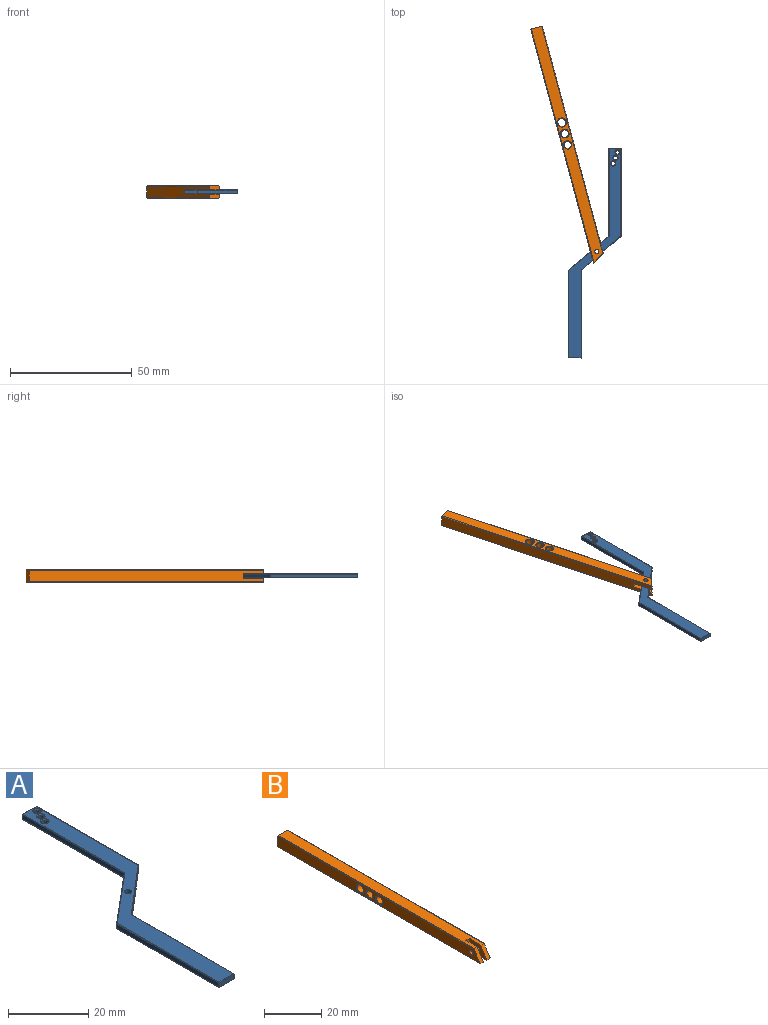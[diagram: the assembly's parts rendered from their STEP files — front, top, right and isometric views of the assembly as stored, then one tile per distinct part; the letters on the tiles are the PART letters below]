
ASSEMBLY  parts=2 mates=1
PART A: 51 faces, bbox 21.7x85.9x1.7 mm
  f0: plane 35.64x1.35mm, normal (1,0,0), area 48mm2, adj f8,f15,f37,f40
  f1: plane 4.92x1.35mm, normal (0.04,1,0), area 6.6mm2, adj f2,f13,f38,f40
  f2: plane 35.89x1.35mm, normal (-1,0,0), area 48.3mm2, adj f1,f11,f32,f36
  f3: plane 16.55x13.86mm, normal (-0.64,0.77,0), area 29.1mm2, adj f12,f25,f31,f32
  f4: plane 35.79x1.35mm, normal (-1,0,0), area 48.2mm2, adj f14,f20,f24,f25
  f5: plane 5.1x1.35mm, normal (0,-1,0), area 6.9mm2, adj f16,f20,f26,f27
  f6: plane 35.86x1.35mm, normal (1,0,0), area 48.3mm2, adj f8,f18,f26,f33
  f7: cylinder r=0.89mm len=1.79mm, axis (0,0,-1), area 9.3mm2, adj f9,f10
  f8: plane 16.32x13.95mm, normal (0.65,-0.76,0), area 28.9mm2, adj f0,f6,f17,f35
  f9: plane 85.62x21.41mm, normal (0,0,1), area 406mm2, adj f7,f24,f27,f31,f33,f34,f35,f36
  f10: plane 85.62x21.41mm, normal (0,0,-1), area 406mm2, adj f7,f11,f12,f13,f14,f15,f16,f17
  f11: cylinder r=0.15mm len=36.03mm, axis (0,-1,0), area 8.6mm2, adj f2,f10,f13,f29
  f12: cylinder r=0.15mm len=16.75mm, axis (-0.77,-0.64,0), area 5.2mm2, adj f3,f10,f21,f29
  f13: cylinder r=0.15mm len=4.92mm, axis (-1,0.04,0), area 1.2mm2, adj f1,f10,f11,f41
  f14: cylinder r=0.15mm len=35.79mm, axis (0,-1,0), area 8.6mm2, adj f4,f10,f19,f21
  f15: cylinder r=0.15mm len=35.64mm, axis (0,1,0), area 8.5mm2, adj f0,f10,f17,f41
  f16: cylinder r=0.15mm len=5.1mm, axis (1,0,0), area 1.2mm2, adj f5,f10,f19,f22
  f17: cylinder r=0.15mm len=16.47mm, axis (0.76,0.65,0), area 5.1mm2, adj f8,f10,f15,f18
  f18: cylinder r=0.15mm len=35.93mm, axis (0,1,0), area 8.6mm2, adj f6,f10,f17,f22
  f19: sphere r=0.15mm, area 0mm2, adj f14,f16,f20
  f20: cylinder r=0.15mm len=1.35mm, axis (0,0,-1), area 0.3mm2, adj f4,f5,f19,f23
  f21: sphere r=0.15mm, area 0mm2, adj f12,f14,f25
  f22: sphere r=0.15mm, area 0mm2, adj f16,f18,f26
  f23: sphere r=0.15mm, area 0mm2, adj f20,f24,f27
  f24: cylinder r=0.15mm len=35.79mm, axis (0,1,0), area 8.6mm2, adj f4,f9,f23,f28
  f25: cylinder r=0.15mm len=1.35mm, axis (0,0,-1), area 0.2mm2, adj f3,f4,f21,f28
  f26: cylinder r=0.15mm len=1.35mm, axis (0,0,-1), area 0.3mm2, adj f5,f6,f22,f30
  f27: cylinder r=0.15mm len=5.1mm, axis (-1,0,0), area 1.2mm2, adj f5,f9,f23,f30
  f28: sphere r=0.15mm, area 0mm2, adj f24,f25,f31
  f29: bspline ~0.21x0.17mm, area 0mm2, adj f11,f12,f32
  f30: sphere r=0.15mm, area 0mm2, adj f26,f27,f33
  f31: cylinder r=0.15mm len=16.64mm, axis (0.77,0.64,0), area 5.2mm2, adj f3,f9,f28,f34
  f32: cylinder r=0.15mm len=1.35mm, axis (0,0,1), area 0.2mm2, adj f2,f3,f29,f34
  f33: cylinder r=0.15mm len=35.93mm, axis (0,-1,0), area 8.6mm2, adj f6,f9,f30,f35
  f34: torus R=0.3mm, axis (0,0,1), area 0mm2, adj f9,f31,f32,f36
  f35: cylinder r=0.15mm len=16.47mm, axis (-0.76,-0.65,0), area 5.1mm2, adj f8,f9,f33,f37
  f36: cylinder r=0.15mm len=35.89mm, axis (0,1,0), area 8.6mm2, adj f2,f9,f34,f38
  f37: cylinder r=0.15mm len=35.64mm, axis (0,-1,0), area 8.5mm2, adj f0,f9,f35,f39
  f38: cylinder r=0.15mm len=4.92mm, axis (1,-0.04,0), area 1.2mm2, adj f1,f9,f36,f39
  f39: sphere r=0.15mm, area 0mm2, adj f37,f38,f40
  f40: cylinder r=0.15mm len=1.35mm, axis (0,0,-1), area 0.3mm2, adj f0,f1,f39,f41
  f41: sphere r=0.15mm, area 0mm2, adj f13,f15,f40
  f42: cylinder r=0.82mm len=1.65mm, axis (0,0,1), area 5.9mm2, adj f45,f50
  f43: cylinder r=0.81mm len=1.62mm, axis (0,0,1), area 5.8mm2, adj f46,f49
  f44: cylinder r=0.8mm len=1.61mm, axis (0,0,1), area 5.8mm2, adj f47,f48
  f45: torus R=1.08mm, axis (0,0,1), area 2.3mm2, adj f9,f42
  f46: torus R=1.06mm, axis (0,0,1), area 2.3mm2, adj f9,f43
  f47: torus R=1.06mm, axis (0,0,1), area 2.2mm2, adj f9,f44
  f48: torus R=1.06mm, axis (0,0,1), area 2.2mm2, adj f10,f44
  f49: torus R=1.06mm, axis (0,0,1), area 2.3mm2, adj f10,f43
  f50: torus R=1.08mm, axis (0,0,1), area 2.3mm2, adj f10,f42
PART B: 25 faces, bbox 5x99.5x5 mm
  f0: plane 99.32x4.45mm, normal (-1,0,0), area 402.8mm2, adj f2,f8,f10,f15,f16,f17,f22,f24
  f1: plane 99.32x4.45mm, normal (1,0,0), area 402.8mm2, adj f2,f9,f11,f18,f19,f20,f21,f23
  f2: plane 4.95x4.95mm, normal (0,1,0), area 24.5mm2, adj f0,f1,f3,f4,f21,f22,f23,f24
  f3: plane 96.46x4.44mm, normal (0,0,1), area 419.1mm2, adj f2,f5,f6,f7,f8,f9,f23,f24
  f4: plane 99.48x4.44mm, normal (0,0,-1), area 427.5mm2, adj f2,f5,f6,f7,f8,f9,f21,f22
  f5: plane 8.69x4.95mm, normal (-1,0,0), area 33.1mm2, adj f3,f4,f6,f9,f11
  f6: plane 4.95x1.67mm, normal (0,-1,0), area 8.3mm2, adj f3,f4,f5,f7
  f7: plane 8.69x4.95mm, normal (1,0,0), area 33.1mm2, adj f3,f4,f6,f8,f10
  f8: plane 4.95x3.01mm, normal (0,-0.85,0.52), area 9.5mm2, adj f0,f3,f4,f7,f22,f24
  f9: plane 4.95x3.01mm, normal (0,-0.85,0.52), area 9.5mm2, adj f1,f3,f4,f5,f21,f23
  f10: cylinder r=0.89mm len=1.78mm, axis (-1,0,0), area 9.2mm2, adj f0,f7
  f11: cylinder r=0.89mm len=1.78mm, axis (-1,0,0), area 9.2mm2, adj f1,f5
  f12: cylinder r=1.46mm len=4.44mm, axis (1,0,0), area 40.7mm2, adj f17,f18
  f13: cylinder r=1.52mm len=4.44mm, axis (1,0,0), area 42.4mm2, adj f16,f19
  f14: cylinder r=1.63mm len=4.44mm, axis (1,0,0), area 45.4mm2, adj f15,f20
  f15: torus R=1.88mm, axis (-1,0,0), area 4.3mm2, adj f0,f14
  f16: torus R=1.77mm, axis (-1,0,0), area 4mm2, adj f0,f13
  f17: torus R=1.71mm, axis (-1,0,0), area 3.9mm2, adj f0,f12
  f18: torus R=1.71mm, axis (-1,0,0), area 3.9mm2, adj f1,f12
  f19: torus R=1.77mm, axis (-1,0,0), area 4mm2, adj f1,f13
  f20: torus R=1.88mm, axis (-1,0,0), area 4.3mm2, adj f1,f14
  f21: cylinder r=0.25mm len=99.48mm, axis (0,1,0), area 39.7mm2, adj f1,f2,f4,f9
  f22: cylinder r=0.25mm len=99.48mm, axis (0,-1,0), area 39.7mm2, adj f0,f2,f4,f8
  f23: cylinder r=0.25mm len=96.62mm, axis (0,-1,0), area 38.5mm2, adj f1,f2,f3,f9
  f24: cylinder r=0.25mm len=96.62mm, axis (0,1,0), area 38.5mm2, adj f0,f2,f3,f8
PLACE A rot(axis=(-0.44,-0.75,-0.49),0deg) t=(-49.52,-11.92,-13.13)mm
PLACE B rot(axis=(-0.13,0.98,0.13),91deg) t=(-73.75,31.67,-12.31)mm
MATE revolute B.f10 <-> A.f7  axis (0,0,1) through (-59.55,-11.48,-11.48)mm
